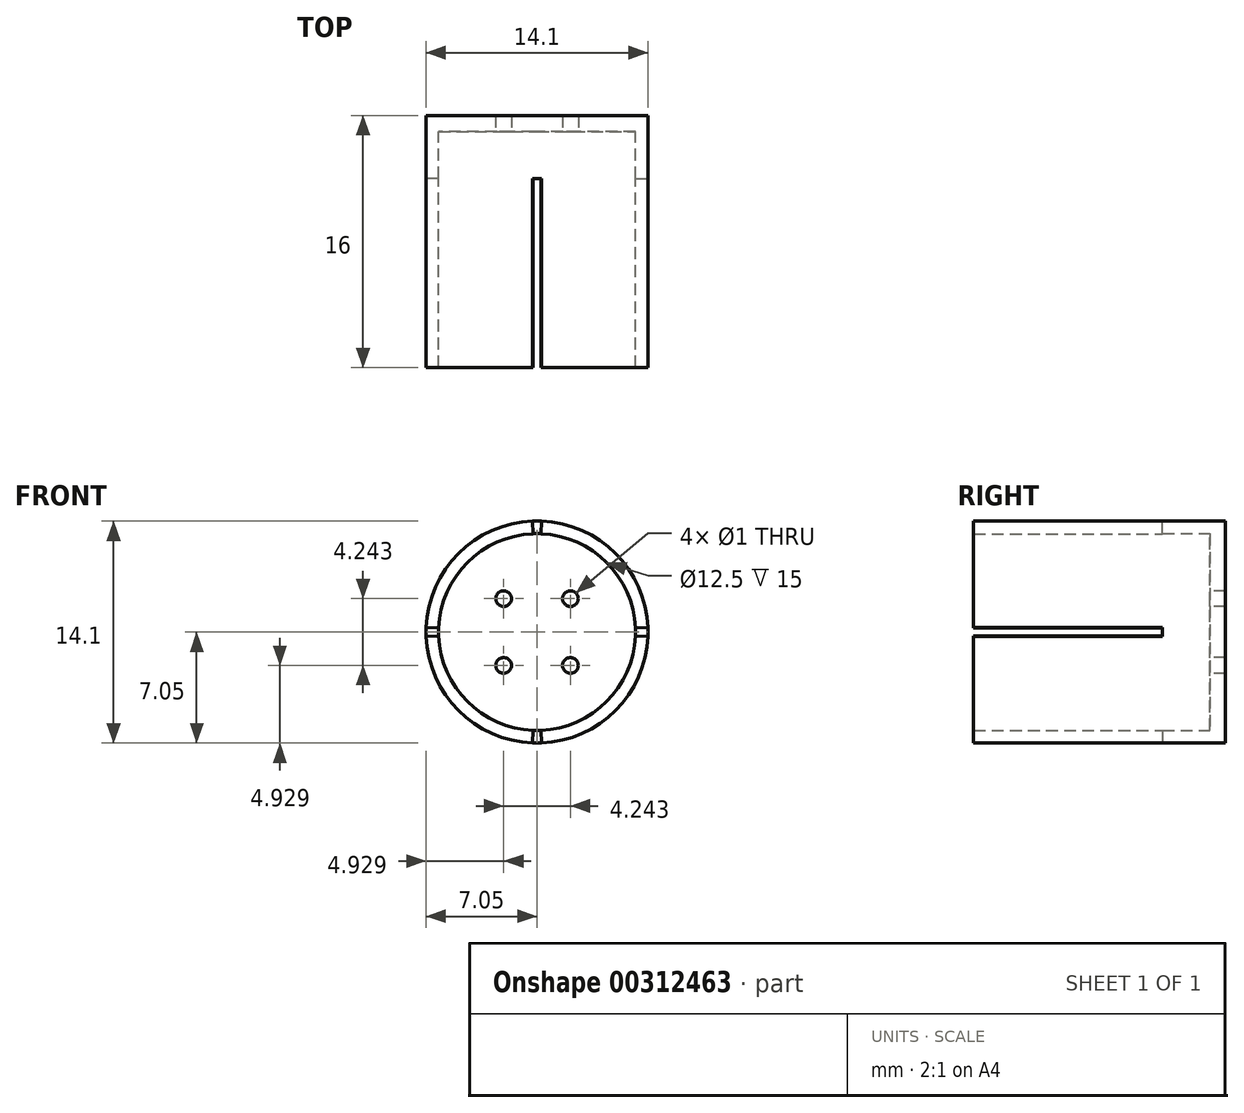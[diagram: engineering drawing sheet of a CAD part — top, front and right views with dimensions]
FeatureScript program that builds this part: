
annotation { "Feature Type Name" : "Feature", "Feature Type Description" : "" }
export const myFeature = defineFeature(function(context is Context, id is Id, definition is map)
    precondition{}
    {
        {
            var Q0;
            Q0=qCreatedBy(makeId("Front.planeOp"),FACE);
            var sketch = newSketch(context, id + "F0", { "sketchPlane" : qUnion([Q0])});
            skArc(sketch, "E0", {"start": v(6.24, 0.25) * mm, "mid": v(4.42, 4.42) * mm, "end": v(0.25, 6.24) * mm});
            skCircle(sketch, "E1.0", {"center": v(0, 0) * mm, "radius": 7.05 * mm});
            skLineSegment(sketch, "E2", {"start": v(0, 0) * mm, "end": v(-7.16, 7.16) * mm, "construction": true});
            skCircle(sketch, "E3", {"center": v(-2.12, 2.12) * mm, "radius": 0.5 * mm});
            skCircle(sketch, "E4.1.0", {"center": v(-2.12, -2.12) * mm, "radius": 0.5 * mm});
            skCircle(sketch, "E4.2.0", {"center": v(2.12, -2.12) * mm, "radius": 0.5 * mm});
            skCircle(sketch, "E4.3.0", {"center": v(2.12, 2.12) * mm, "radius": 0.5 * mm});
            skLineSegment(sketch, "E5", {"start": v(6.24, 0.25) * mm, "end": v(7.04, 0.28) * mm});
            skLineSegment(sketch, "E6.MirrorCS", {"start": v(6.24, -0.25) * mm, "end": v(7.04, -0.28) * mm});
            skLineSegment(sketch, "E7.1.0", {"start": v(-0.25, 6.24) * mm, "end": v(-0.28, 7.04) * mm});
            skLineSegment(sketch, "E7.1.1", {"start": v(0.25, 6.24) * mm, "end": v(0.28, 7.04) * mm});
            skLineSegment(sketch, "E7.2.0", {"start": v(-6.24, -0.25) * mm, "end": v(-7.04, -0.28) * mm});
            skLineSegment(sketch, "E7.2.1", {"start": v(-6.24, 0.25) * mm, "end": v(-7.04, 0.28) * mm});
            skLineSegment(sketch, "E7.3.0", {"start": v(0.25, -6.24) * mm, "end": v(0.28, -7.04) * mm});
            skLineSegment(sketch, "E7.3.1", {"start": v(-0.25, -6.24) * mm, "end": v(-0.28, -7.04) * mm});
            skArc(sketch, "E8.trimOffspring", {"start": v(0.25, -6.24) * mm, "mid": v(4.42, -4.42) * mm, "end": v(6.24, -0.25) * mm});
            skArc(sketch, "E9.trimOffspring", {"start": v(-6.24, -0.25) * mm, "mid": v(-4.42, -4.42) * mm, "end": v(-0.25, -6.24) * mm});
            skArc(sketch, "E10.trimOffspring", {"start": v(-0.25, 6.24) * mm, "mid": v(-4.42, 4.42) * mm, "end": v(-6.24, 0.25) * mm});
            skCircle(sketch, "E11", {"center": v(0, 0) * mm, "radius": 6.25 * mm});
            skSolve(sketch);
        }
        {
            var Q0;
            {var subQ0=sQuery(id+"F0.wireOp",EDGE,"E7.1.0");Q0=makeQuery(id+"F0.imprint","IMPRINT",FACE,{"disambiguationData":[TD([[makeQuery(id+"F0.imprint","IMPRINT",EDGE,{"derivedFrom":subQ0}),1.0]])]});}
            var Q1;
            {var subQ0=sQuery(id+"F0.wireOp",EDGE,"E7.1.0");Q1=makeQuery(id+"F0.imprint","IMPRINT",FACE,{"disambiguationData":[TD([[makeQuery(id+"F0.imprint","IMPRINT",EDGE,{"derivedFrom":subQ0}),-1.0]])]});}
            var Q2;
            Q2=makeQuery(id+"F0.imprint","IMPRINT",FACE,{"disambiguationData":[TD([[makeQuery(id+"F0.imprint","IMPRINT",EDGE,{"derivedFrom":sQuery(id+"F0.wireOp",EDGE,"E3")}),-1.0]])]});
            var Q3;
            {var subQ0=sQuery(id+"F0.wireOp",EDGE,"E5");Q3=makeQuery(id+"F0.imprint","IMPRINT",FACE,{"disambiguationData":[TD([[makeQuery(id+"F0.imprint","IMPRINT",EDGE,{"derivedFrom":subQ0}),1.0]])]});}
            var Q4;
            {var subQ0=sQuery(id+"F0.wireOp",EDGE,"E5");Q4=makeQuery(id+"F0.imprint","IMPRINT",FACE,{"disambiguationData":[TD([[makeQuery(id+"F0.imprint","IMPRINT",EDGE,{"derivedFrom":subQ0}),-1.0]])]});}
            var Q5;
            {var subQ0=sQuery(id+"F0.wireOp",EDGE,"E6.MirrorCS");Q5=makeQuery(id+"F0.imprint","IMPRINT",FACE,{"disambiguationData":[TD([[makeQuery(id+"F0.imprint","IMPRINT",EDGE,{"derivedFrom":subQ0}),-1.0]])]});}
            var Q6;
            {var subQ0=sQuery(id+"F0.wireOp",EDGE,"E7.3.0");Q6=makeQuery(id+"F0.imprint","IMPRINT",FACE,{"disambiguationData":[TD([[makeQuery(id+"F0.imprint","IMPRINT",EDGE,{"derivedFrom":subQ0}),-1.0]])]});}
            var Q7;
            {var subQ0=sQuery(id+"F0.wireOp",EDGE,"E7.2.0");Q7=makeQuery(id+"F0.imprint","IMPRINT",FACE,{"disambiguationData":[TD([[makeQuery(id+"F0.imprint","IMPRINT",EDGE,{"derivedFrom":subQ0}),1.0]])]});}
            var Q8;
            {var subQ0=sQuery(id+"F0.wireOp",EDGE,"E7.2.0");Q8=makeQuery(id+"F0.imprint","IMPRINT",FACE,{"disambiguationData":[TD([[makeQuery(id+"F0.imprint","IMPRINT",EDGE,{"derivedFrom":subQ0}),-1.0]])]});}
            extrude(context, id + "F1", {"entities" : qUnion([Q0, Q1, Q2, Q3, Q4, Q5, Q6, Q7, Q8]), "depth" : -1 * mm, "offsetDistance" : 25 * mm});
        }
        {
            var Q0;
            {var subQ0=sQuery(id+"F0.wireOp",EDGE,"E7.1.0");Q0=makeQuery(id+"F0.imprint","IMPRINT",FACE,{"disambiguationData":[TD([[makeQuery(id+"F0.imprint","IMPRINT",EDGE,{"derivedFrom":subQ0}),1.0]])]});}
            var Q1;
            {var subQ0=sQuery(id+"F0.wireOp",EDGE,"E5");Q1=makeQuery(id+"F0.imprint","IMPRINT",FACE,{"disambiguationData":[TD([[makeQuery(id+"F0.imprint","IMPRINT",EDGE,{"derivedFrom":subQ0}),1.0]])]});}
            var Q2;
            {var subQ0=sQuery(id+"F0.wireOp",EDGE,"E6.MirrorCS");Q2=makeQuery(id+"F0.imprint","IMPRINT",FACE,{"disambiguationData":[TD([[makeQuery(id+"F0.imprint","IMPRINT",EDGE,{"derivedFrom":subQ0}),-1.0]])]});}
            var Q3;
            {var subQ0=sQuery(id+"F0.wireOp",EDGE,"E7.2.0");Q3=makeQuery(id+"F0.imprint","IMPRINT",FACE,{"disambiguationData":[TD([[makeQuery(id+"F0.imprint","IMPRINT",EDGE,{"derivedFrom":subQ0}),1.0]])]});}
            extrude(context, id + "F2", {"entities" : qUnion([Q0, Q1, Q2, Q3]), "operationType" : NewBodyOperationType.ADD, "depth" : 15 * mm, "offsetDistance" : 25 * mm});
        }
        {
            var Q0;
            {var subQ0=sQuery(id+"F0.wireOp",EDGE,"E7.2.0");Q0=makeQuery(id+"F0.imprint","IMPRINT",FACE,{"disambiguationData":[TD([[makeQuery(id+"F0.imprint","IMPRINT",EDGE,{"derivedFrom":subQ0}),-1.0]])]});}
            var Q1;
            {var subQ0=sQuery(id+"F0.wireOp",EDGE,"E7.3.0");Q1=makeQuery(id+"F0.imprint","IMPRINT",FACE,{"disambiguationData":[TD([[makeQuery(id+"F0.imprint","IMPRINT",EDGE,{"derivedFrom":subQ0}),-1.0]])]});}
            var Q2;
            {var subQ0=sQuery(id+"F0.wireOp",EDGE,"E5");Q2=makeQuery(id+"F0.imprint","IMPRINT",FACE,{"disambiguationData":[TD([[makeQuery(id+"F0.imprint","IMPRINT",EDGE,{"derivedFrom":subQ0}),-1.0]])]});}
            var Q3;
            {var subQ0=sQuery(id+"F0.wireOp",EDGE,"E7.1.0");Q3=makeQuery(id+"F0.imprint","IMPRINT",FACE,{"disambiguationData":[TD([[makeQuery(id+"F0.imprint","IMPRINT",EDGE,{"derivedFrom":subQ0}),-1.0]])]});}
            extrude(context, id + "F3", {"entities" : qUnion([Q0, Q1, Q2, Q3]), "operationType" : NewBodyOperationType.ADD, "depth" : 3 * mm, "offsetDistance" : 25 * mm});
        }
    });
